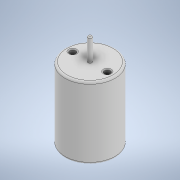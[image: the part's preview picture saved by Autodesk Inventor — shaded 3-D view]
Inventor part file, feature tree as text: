
AUTODESK INVENTOR PART (.ipt)
format: ipt  version: 2020.2 (Build 242310000, 310)  size: 142,336 bytes
history: native  units: mm
features: extrude x3, sketch x3, fillet x1
ambient origin geometry x8: Origin, YZ Plane, XZ Plane, XY Plane, X Axis, Y Axis, Z Axis, Center Point
bodies: Solid1 (feature_tree)
feature tree (7):
  extrude  "Extrusion1"  Depth=35.2mm TaperAngle=0.0deg
  extrude  "Extrusion2"  Depth=11.0mm TaperAngle=0.0deg
  extrude  "Extrusion3"  Depth=0.5mm
  fillet  "Fillet1"  Radius=20.0mm
  sketch  "Sketch2"  dims[d1=24.6mm d2=35.2mm d3=0.0mm]
  sketch  "Sketch3"  dims[d4=2.0mm d5=11.0mm d6=0.0mm]
  sketch  "Sketch4"  dims[d7=3.0mm d9=8.5mm d11=20.0mm d13=360.0deg d15=17.0mm d16=0.0mm d17=1.0mm d18=0.5mm]
